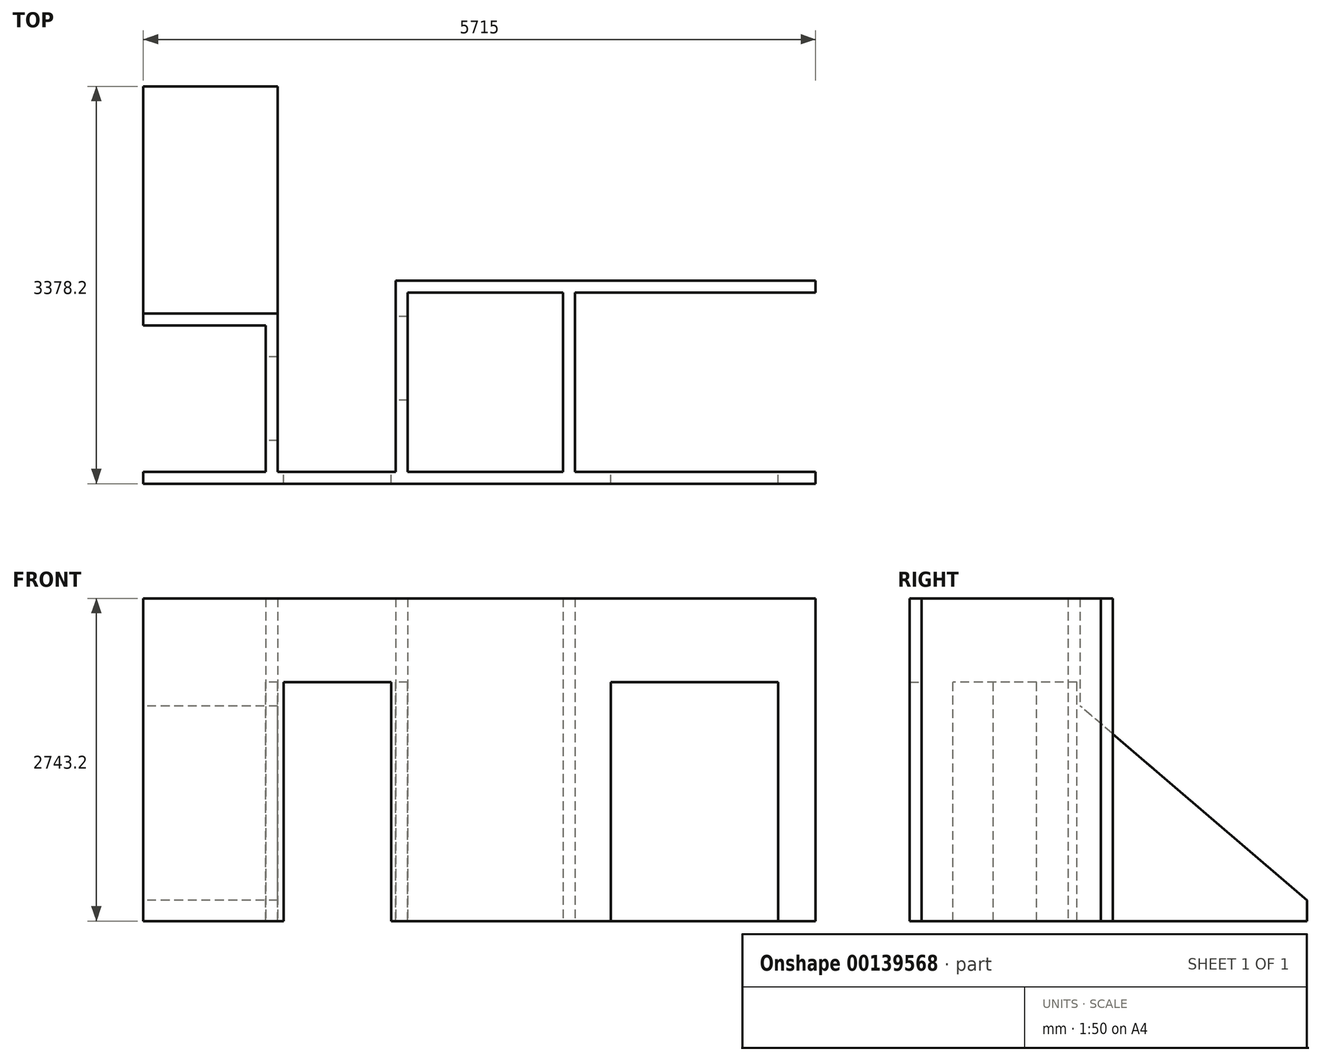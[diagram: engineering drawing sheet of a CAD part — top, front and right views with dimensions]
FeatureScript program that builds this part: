
annotation { "Feature Type Name" : "Feature", "Feature Type Description" : "" }
export const myFeature = defineFeature(function(context is Context, id is Id, definition is map)
    precondition{}
    {
        {
            var Q0;
            Q0=qCreatedBy(makeId("Top.planeOp"),FACE);
            var sketch = newSketch(context, id + "F0", { "sketchPlane" : qUnion([Q0])});
            skLineSegment(sketch, "E0.bottom", {"start": v(-2857.5, 5778.5) * mm, "end": v(2857.5, 5778.5) * mm});
            skLineSegment(sketch, "E0.top", {"start": v(-2857.5, -5778.5) * mm, "end": v(2857.5, -5778.5) * mm});
            skLineSegment(sketch, "E0.left", {"start": v(-2857.5, 5778.5) * mm, "end": v(-2857.5, -5778.5) * mm});
            skLineSegment(sketch, "E0.right", {"start": v(2857.5, 5778.5) * mm, "end": v(2857.5, -5778.5) * mm});
            skLineSegment(sketch, "E1", {"start": v(-2857.5, -139.7) * mm, "end": v(2857.5, -139.7) * mm});
            skLineSegment(sketch, "E2", {"start": v(-2857.5, -38.1) * mm, "end": v(-1816.1, -38.1) * mm});
            skLineSegment(sketch, "E3", {"start": v(-1816.1, -38.1) * mm, "end": v(-1816.1, 1206.5) * mm});
            skLineSegment(sketch, "E4", {"start": v(-1816.1, 1206.5) * mm, "end": v(-2857.5, 1206.5) * mm});
            skLineSegment(sketch, "E5", {"start": v(-2857.5, 1308.1) * mm, "end": v(-1714.5, 1308.1) * mm});
            skLineSegment(sketch, "E6", {"start": v(-1714.5, 1308.1) * mm, "end": v(-1714.5, -38.1) * mm});
            skLineSegment(sketch, "E7", {"start": v(-1714.5, -38.1) * mm, "end": v(-711.2, -38.1) * mm});
            skLineSegment(sketch, "E8", {"start": v(-711.2, -38.1) * mm, "end": v(-711.2, 1587.5) * mm});
            skLineSegment(sketch, "E9", {"start": v(-711.2, 1587.5) * mm, "end": v(2857.5, 1587.5) * mm});
            skLineSegment(sketch, "E10.bottom", {"start": v(-609.6, 1485.9) * mm, "end": v(711.2, 1485.9) * mm});
            skLineSegment(sketch, "E10.top", {"start": v(-609.6, -38.1) * mm, "end": v(711.2, -38.1) * mm});
            skLineSegment(sketch, "E10.left", {"start": v(-609.6, 1485.9) * mm, "end": v(-609.6, -38.1) * mm});
            skLineSegment(sketch, "E10.right", {"start": v(711.2, 1485.9) * mm, "end": v(711.2, -38.1) * mm});
            skLineSegment(sketch, "E11", {"start": v(2857.5, 1485.9) * mm, "end": v(812.8, 1485.9) * mm});
            skLineSegment(sketch, "E12", {"start": v(812.8, 1485.9) * mm, "end": v(812.8, -38.1) * mm});
            skLineSegment(sketch, "E13", {"start": v(812.8, -38.1) * mm, "end": v(2857.5, -38.1) * mm});
            skSolve(sketch);
        }
        {
            var Q0;
            {var subQ4=sQuery(id+"F0.wireOp",EDGE,"E1");Q0=makeQuery(id+"F0.imprint","IMPRINT",FACE,{"disambiguationData":[TD([[makeQuery(id+"F0.imprint","IMPRINT",EDGE,{"derivedFrom":subQ4}),1.0]])]});}
            extrude(context, id + "F1", {"entities" : qUnion([Q0]), "depth" : 2743.2 * mm});
        }
        {
            var Q0;
            Q0=makeQuery(id+"F1.opExtrude","SWEPT_FACE",FACE,{"disambiguationData":[OSD([sQuery(id+"F0.wireOp",EDGE,"E13")])]});
            var sketch = newSketch(context, id + "F2", { "sketchPlane" : qUnion([Q0])});
            skLineSegment(sketch, "E14.bottom", {"start": v(-2540, 0) * mm, "end": v(-1117.6, 0) * mm});
            skLineSegment(sketch, "E14.top", {"start": v(-2540, 2032) * mm, "end": v(-1117.6, 2032) * mm});
            skLineSegment(sketch, "E14.left", {"start": v(-2540, 0) * mm, "end": v(-2540, 2032) * mm});
            skLineSegment(sketch, "E14.right", {"start": v(-1117.6, 0) * mm, "end": v(-1117.6, 2032) * mm});
            skSolve(sketch);
        }
        {
            var Q0;
            Q0 = qSketchRegion(id + "F2", true);
            extrude(context, id + "F3", {"entities" : qUnion([Q0]), "operationType" : NewBodyOperationType.REMOVE, "oppositeDirection" : true, "depth" : 101.6 * mm});
        }
        {
            var Q0;
            Q0=makeQuery(id+"F1.opExtrude","SWEPT_FACE",FACE,{"disambiguationData":[OSD([sQuery(id+"F0.wireOp",EDGE,"E8")])]});
            var sketch = newSketch(context, id + "F4", { "sketchPlane" : qUnion([Q0])});
            skLineSegment(sketch, "E15.bottom", {"start": v(-1282.7, 0) * mm, "end": v(-571.5, 0) * mm});
            skLineSegment(sketch, "E15.top", {"start": v(-1282.7, 2032) * mm, "end": v(-571.5, 2032) * mm});
            skLineSegment(sketch, "E15.left", {"start": v(-1282.7, 0) * mm, "end": v(-1282.7, 2032) * mm});
            skLineSegment(sketch, "E15.right", {"start": v(-571.5, 0) * mm, "end": v(-571.5, 2032) * mm});
            skSolve(sketch);
        }
        {
            var Q0;
            Q0 = qSketchRegion(id + "F4", true);
            extrude(context, id + "F5", {"entities" : qUnion([Q0]), "operationType" : NewBodyOperationType.REMOVE, "oppositeDirection" : true, "depth" : 101.6 * mm});
        }
        {
            var Q0;
            Q0=makeQuery(id+"F1.opExtrude","SWEPT_FACE",FACE,{"disambiguationData":[OSD([sQuery(id+"F0.wireOp",EDGE,"E7")])]});
            var sketch = newSketch(context, id + "F6", { "sketchPlane" : qUnion([Q0])});
            skLineSegment(sketch, "E16.bottom", {"start": v(749.3, 0) * mm, "end": v(1663.7, 0) * mm});
            skLineSegment(sketch, "E16.top", {"start": v(749.3, 2032) * mm, "end": v(1663.7, 2032) * mm});
            skLineSegment(sketch, "E16.left", {"start": v(749.3, 0) * mm, "end": v(749.3, 2032) * mm});
            skLineSegment(sketch, "E16.right", {"start": v(1663.7, 0) * mm, "end": v(1663.7, 2032) * mm});
            skSolve(sketch);
        }
        {
            var Q0;
            Q0 = qSketchRegion(id + "F6", true);
            extrude(context, id + "F7", {"entities" : qUnion([Q0]), "operationType" : NewBodyOperationType.REMOVE, "oppositeDirection" : true, "depth" : 101.6 * mm});
        }
        {
            var Q0;
            Q0=makeQuery(id+"F1.opExtrude","SWEPT_FACE",FACE,{"disambiguationData":[OSD([sQuery(id+"F0.wireOp",EDGE,"E3")])]});
            var sketch = newSketch(context, id + "F8", { "sketchPlane" : qUnion([Q0])});
            skLineSegment(sketch, "E17.bottom", {"start": v(-939.8, 0) * mm, "end": v(-228.6, 0) * mm});
            skLineSegment(sketch, "E17.top", {"start": v(-939.8, 2032) * mm, "end": v(-228.6, 2032) * mm});
            skLineSegment(sketch, "E17.left", {"start": v(-939.8, 0) * mm, "end": v(-939.8, 2032) * mm});
            skLineSegment(sketch, "E17.right", {"start": v(-228.6, 0) * mm, "end": v(-228.6, 2032) * mm});
            skSolve(sketch);
        }
        {
            var Q0;
            Q0 = qSketchRegion(id + "F8", true);
            extrude(context, id + "F9", {"entities" : qUnion([Q0]), "operationType" : NewBodyOperationType.REMOVE, "oppositeDirection" : true, "depth" : 101.6 * mm});
        }
        {
            var Q0;
            {var subQ0=sQuery(id+"F0.wireOp",EDGE,"E0.left");Q0=makeQuery(id+"F1.opExtrude","SWEPT_FACE",FACE,{"disambiguationData":[OSD([subQ0]),TDD([makeQuery(id+"F0.imprint","IMPRINT",EDGE,{"disambiguationData":[TD([[makeQuery(id+"F0.imprint","INTERSECT",VERTEX,{"derivedFrom":[subQ0,sQuery(id+"F0.wireOp",EDGE,"E4")]}),1.0]])],"derivedFrom":subQ0})])]});}
            var sketch = newSketch(context, id + "F10", { "sketchPlane" : qUnion([Q0])});
            skLineSegment(sketch, "E18", {"start": v(-1308.1, 0) * mm, "end": v(-3238.5, 0) * mm});
            skLineSegment(sketch, "E19", {"start": v(-3238.5, 0) * mm, "end": v(-3238.5, 177.8) * mm});
            skLineSegment(sketch, "E20", {"start": v(-3238.5, 177.8) * mm, "end": v(-1308.1, 1828.8) * mm});
            skLineSegment(sketch, "E21", {"start": v(-1308.1, 1828.8) * mm, "end": v(-1308.1, 0) * mm});
            skSolve(sketch);
        }
        {
            var Q0;
            Q0 = qSketchRegion(id + "F10", true);
            var Q1;
            Q1=makeQuery(id+"F1.opExtrude","SWEPT_FACE",FACE,{"disambiguationData":[OSD([sQuery(id+"F0.wireOp",EDGE,"E6")])]});
            extrude(context, id + "F11", {"entities" : qUnion([Q0]), "operationType" : NewBodyOperationType.ADD, "endBound" : BoundingType.UP_TO_SURFACE, "oppositeDirection" : true, "endBoundEntityFace" : qUnion([Q1]), "depth" : 1078.42 * mm});
        }
    });
